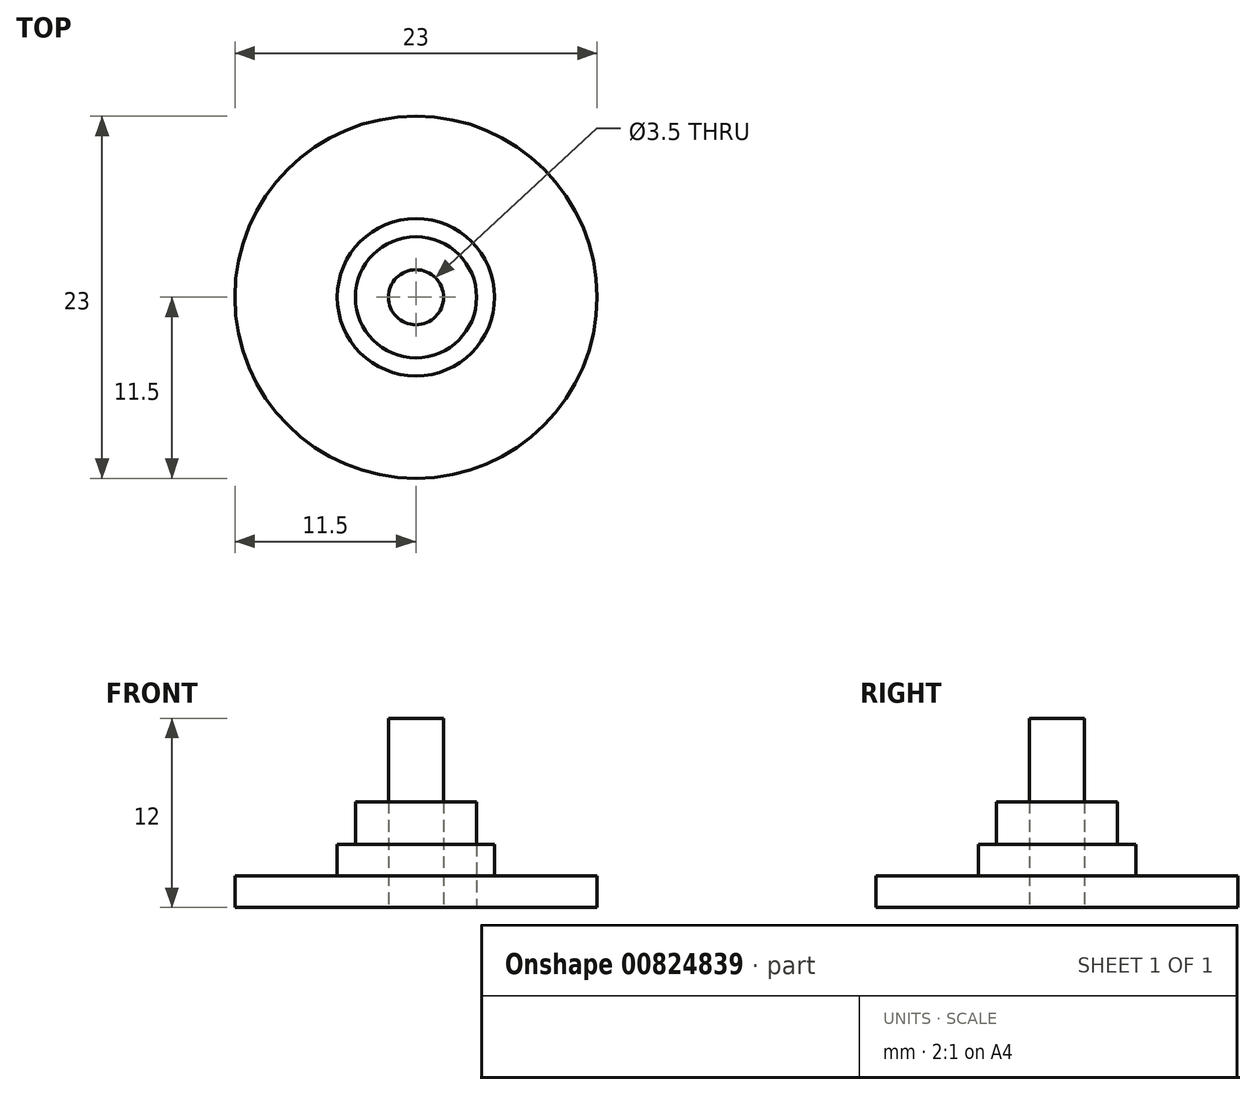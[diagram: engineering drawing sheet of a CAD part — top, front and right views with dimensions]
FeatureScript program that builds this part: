
annotation { "Feature Type Name" : "Feature", "Feature Type Description" : "" }
export const myFeature = defineFeature(function(context is Context, id is Id, definition is map)
    precondition{}
    {
        {
            var Q0;
            Q0=qCreatedBy(makeId("Top.planeOp"),FACE);
            var sketch = newSketch(context, id + "F0", { "sketchPlane" : qUnion([Q0])});
            skCircle(sketch, "E0", {"center": v(0, 0) * mm, "radius": 11.5 * mm});
            skCircle(sketch, "E1", {"center": v(0, 0) * mm, "radius": 3.85 * mm});
            skCircle(sketch, "E2", {"center": v(0, 0) * mm, "radius": 5 * mm});
            skCircle(sketch, "E3", {"center": v(0, 0) * mm, "radius": 1.75 * mm});
            skSolve(sketch);
        }
        {
            var Q0;
            Q0 = qSketchRegion(id + "F0", true);
            extrude(context, id + "F1", {"entities" : qUnion([Q0]), "depth" : 2 * mm, "offsetDistance" : 25 * mm});
        }
        {
            var Q0;
            Q0=makeQuery(id+"F0.imprint","IMPRINT",FACE,{"disambiguationData":[TD([[makeQuery(id+"F0.imprint","IMPRINT",EDGE,{"derivedFrom":sQuery(id+"F0.wireOp",EDGE,"E1")}),-1.0]])]});
            extrude(context, id + "F2", {"entities" : qUnion([Q0]), "operationType" : NewBodyOperationType.ADD, "depth" : 4 * mm, "offsetDistance" : 25 * mm});
        }
        {
            var Q0;
            Q0=makeQuery(id+"F0.imprint","IMPRINT",FACE,{"disambiguationData":[TD([[makeQuery(id+"F0.imprint","IMPRINT",EDGE,{"derivedFrom":sQuery(id+"F0.wireOp",EDGE,"E3")}),1.0]])]});
            extrude(context, id + "F3", {"entities" : qUnion([Q0]), "operationType" : NewBodyOperationType.ADD, "depth" : 12 * mm, "offsetDistance" : 25 * mm});
        }
        {
            var Q0;
            Q0=makeQuery(id+"F0.imprint","IMPRINT",FACE,{"disambiguationData":[TD([[makeQuery(id+"F0.imprint","IMPRINT",EDGE,{"derivedFrom":sQuery(id+"F0.wireOp",EDGE,"E1")}),1.0]])]});
            extrude(context, id + "F4", {"entities" : qUnion([Q0]), "depth" : 6.7 * mm, "offsetDistance" : 25 * mm});
        }
    });
